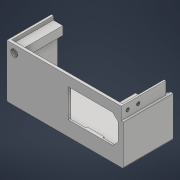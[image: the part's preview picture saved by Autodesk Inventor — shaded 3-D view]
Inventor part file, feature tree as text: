
AUTODESK INVENTOR PART (.ipt)
format: ipt  version: 2021 (Build 250183000, 183)  size: 830,976 bytes
history: native  units: mm
features: extrude x9, sketch x9, projected_geometry x7, thicken_offset x5, other x3, fillet x2, direct_edit x1, move_body x1
ambient origin geometry x8: Origin, YZ Plane, XZ Plane, XY Plane, X Axis, Y Axis, Z Axis, Center Point
bodies: Solid1 (feature_tree)
feature tree (37):
  other  "psu_cover_20a_i3_steel"
  other  "MeshFeature1"
  extrude  "Extrusion1"  Depth=10.0mm TaperAngle=0.0deg
  extrude  "Extrusion2"  Depth=27.0mm
  extrude  "Extrusion3"  Depth=6.0mm
  extrude  "Extrusion4"  Depth=5.0mm
  extrude  "Extrusion5"  Depth=5.0mm
  fillet  "Fillet1"  Radius=10.0mm
  fillet  "Fillet2"  Radius=10.0mm
  extrude  "Extrusion6"  Depth=10.0mm TaperAngle=0.0deg
  extrude  "Extrusion7"  Depth=1.0mm
  thicken_offset  "Thicken1"
  thicken_offset  "Thicken2"
  thicken_offset  "Thicken3"
  thicken_offset  "Thicken4"
  thicken_offset  "Thicken5"
  extrude  "Extrusion8"  Depth=15.0mm
  direct_edit  "Direct Edit1"
  other  "Lip1"
  extrude  "Extrusion9"  Depth=11.0mm
  sketch  "Sketch1"  dims[d0=10.0mm d1=0.0mm d2=10.0mm d3=0.0mm]
  projected_geometry  "Projected Loop1"
  sketch  "Sketch2"  dims[d4=47.0mm d5=27.0mm]
  projected_geometry  "Projected Loop2"
  sketch  "Sketch3"  dims[d6=5.0mm d7=6.0mm]
  sketch  "Sketch4"  dims[d8=5.0mm d9=5.0mm]
  projected_geometry  "Projected Loop3"
  sketch  "Sketch5"  dims[d10=5.0mm d11=5.0mm d12=10.0mm d13=0.0mm d14=10.0mm d15=0.0mm]
  projected_geometry  "Projected Loop4"
  sketch  "Sketch6"  dims[d16=14.0mm d17=10.0mm d18=0.0mm]
  projected_geometry  "Projected Loop5"
  sketch  "Sketch7"  dims[d19=3.0mm d20=1.0mm]
  projected_geometry  "Projected Loop6"
  sketch  "Sketch8"  dims[d21=1.5mm d22=15.0mm]
  projected_geometry  "Projected Loop7"
  sketch  "Sketch9"  dims[d23=15.0mm d24=11.0mm d25=11.0mm d26=1.5mm d27=0.0mm d28=10.0mm d29=0.0mm d30=1.0mm d31=1.0mm d32=0.5mm d33=0.5mm d34=0.5mm d35=0.5mm d36=1.0mm d37=1.0mm d38=1.0mm d39=1.0mm d40=10.0mm d41=0.0mm d42=0.0mm d43=0.0mm d44=-8.0mm d45=7.0mm d46=1.0mm d47=0.0mm d48=0.0mm d49=1.5mm d50=1.0mm d51=0.0mm d52=0.0mm d53=0.0mm d54=0.0mm d55=25.0mm]
  move_body  "Move1"
